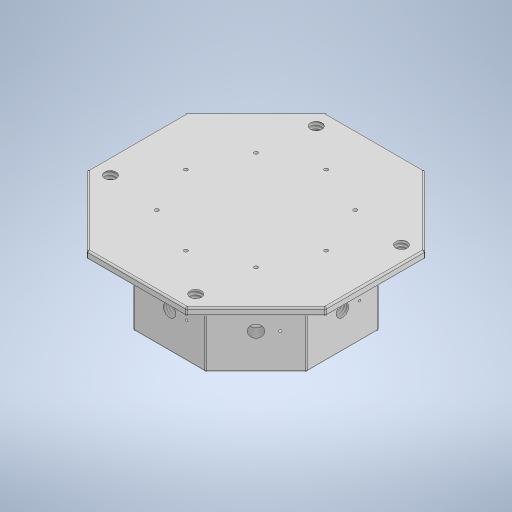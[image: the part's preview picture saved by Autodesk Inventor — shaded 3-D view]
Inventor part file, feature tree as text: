
AUTODESK INVENTOR PART (.ipt)
format: ipt  version: 2024.3 (Build 283343000, 343)  size: 592,896 bytes
history: native  units: in
note: dims shown in document units (in); Inventor stores cm internally (conversion verified against a paired STEP export)
features: hole x9, sketch x8, pattern_circular x5, fillet x5, extrude x2
ambient origin geometry x8: Origin, YZ Plane, XZ Plane, XY Plane, X Axis, Y Axis, Z Axis, Center Point
bodies: Solid1 (feature_tree)
feature tree (29):
  sketch  "Sketch1: base"  dims[d19=0.156in d20=0.38in d21=0.375in d22=0.25in d23=0.5635in d25=0.0in]
  sketch  "Sketch2: top flange"  dims[d27=0.38in d28=0.375in d29=0.25in d30=0.5635in d31=0.1575in d43=0.0in]
  extrude  "Ex1: main body"  TaperAngle=0.0deg  [1 undecoded]
  extrude  "Ex2: top flange"  TaperAngle=0.0deg  [1 undecoded]
  sketch  "Sketch: valve outlet"  dims[d46=0.75in d47=0.375in d48=0.25in d49=0.5635in d50=0.2in d51=0.0in d54=0.75in d55=0.375in d56=0.25in d57=0.5635in]
  hole  "Hole: valve outlet"  [1 undecoded]
  hole  "Hole: valve outlet thread"  [1 undecoded]
  hole  "Hole: clean air in"  [1 undecoded]
  hole  "Hole: valve inlet"  [1 undecoded]
  sketch  "Sketch: odor in"  dims[d59=0.0in]
  hole  "Hole: odor in (to valve)"  [1 undecoded]
  hole  "Hole: odor in (from vial) (NResearch)"  [1 undecoded]
  sketch  "Sketch: Flange screws"  dims[d60=0.211in d61=0.5in d62=0.375in d63=0.25in d64=0.5635in d66=0.0in]
  pattern_circular  "Circular Pattern: air in"  [2 undecoded]
  pattern_circular  "Circular Pattern: output odor"  [2 undecoded]
  pattern_circular  "Circular Pattern: output for Clippard thread"  [2 undecoded]
  pattern_circular  "Circular Pattern: valve inlet, odor in"  [2 undecoded]
  hole  "Hole: Flange screws"  [1 undecoded]
  pattern_circular  "Circular Pattern: Flange screws"  [2 undecoded]
  hole  "Hole: Exhaust"  [1 undecoded]
  hole  "Hole: Exhaust (NResearch)"  [1 undecoded]
  fillet  "Fillet1: flange edges"  Radius=0.75in
  fillet  "Fillet2: flange edges"  Radius=0.8108in
  fillet  "Fillet3: bottom edges"  Radius=0.0625in
  fillet  "Fillet4: outside edges"  Radius=0.75in
  fillet  "Fillet5: outside edges"  Radius=0.375in
  sketch  "Sketch: valve footprint"  dims[d67=0.145in d68=0.38in d69=0.375in d70=0.25in d71=0.5635in d72=0.588in d73=0.0in d84=0.38in d85=0.375in d86=0.25in d87=0.5635in]
  sketch  "Sketch: clean air in"  dims[d88=0.45in d89=0.0in d136=0.75in d137=0.375in d138=0.25in d139=0.5635in]
  sketch  "Sketch: valve inlet"  dims[d141=0.0in d153=0.211in d154=0.5in d155=0.375in d156=0.25in d157=0.5635in d159=0.0in d144=0.0in d145=0.0in d146=0.0in d147=0.0in d164=1.0in d165=1.0in d166=0.45in d167=0.15in d168=0.046in d169=0.375in d170=0.5635in d171=0.75in d172=0.8108in d173=0.0625in d174=0.75in d175=0.375in d176=0.375in d177=0.5635in d178=0.75in d179=0.8108in d180=0.0625in d181=0.75in d182=0.375in]
note: 21 required parameter values undecoded (feature->parameter linkage not recoverable at this tier; creation-order binding heuristic only, values carry confidence <= 0.55)
